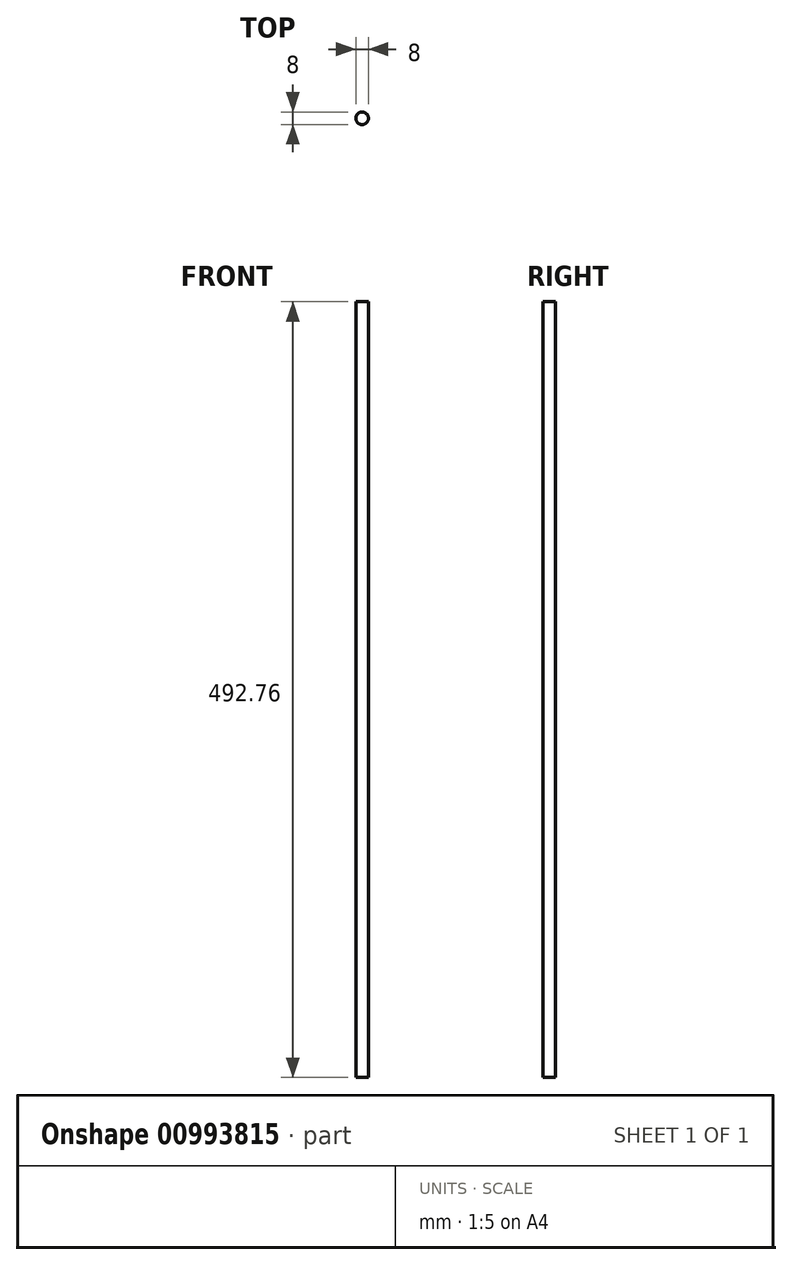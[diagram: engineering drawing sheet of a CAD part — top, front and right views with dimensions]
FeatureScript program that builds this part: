
annotation { "Feature Type Name" : "Feature", "Feature Type Description" : "" }
export const myFeature = defineFeature(function(context is Context, id is Id, definition is map)
    precondition{}
    {
        {
            var Q0;
            Q0=qCreatedBy(makeId("Top.planeOp"),FACE);
            var sketch = newSketch(context, id + "F0", { "sketchPlane" : qUnion([Q0])});
            skCircle(sketch, "E0", {"center": v(0, 0) * mm, "radius": 4 * mm});
            skSolve(sketch);
        }
        {
            var Q0;
            Q0=qSketchRegion(id+"F0",true);
            extrude(context, id + "F1", {"entities" : qUnion([Q0]), "depth" : 492.75 * mm, "offsetDistance" : 25 * mm, "symmetric" : true});
        }
    });
